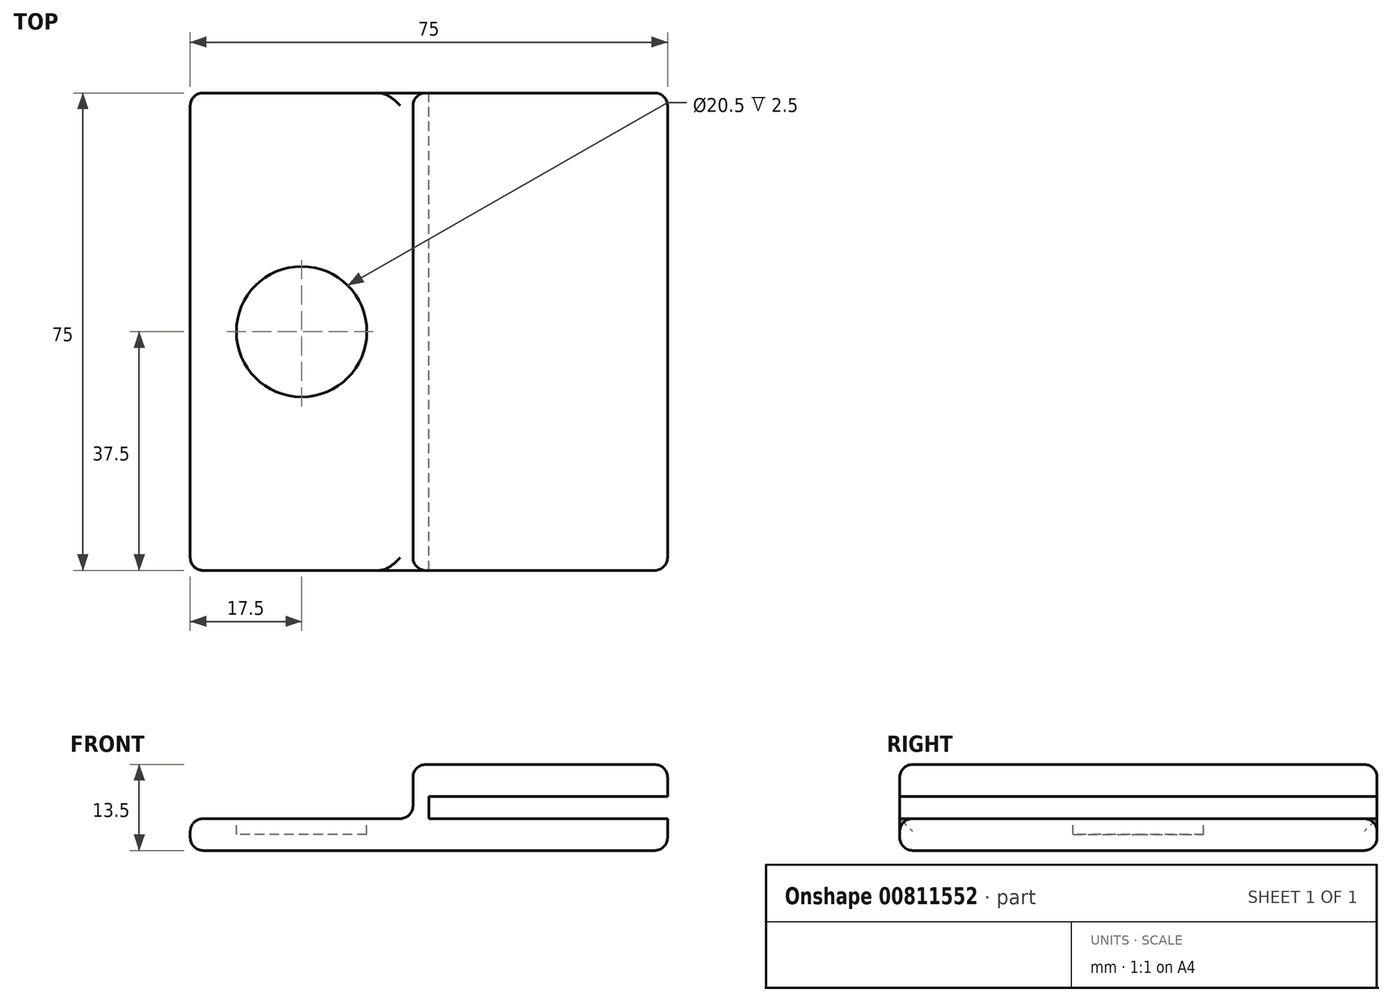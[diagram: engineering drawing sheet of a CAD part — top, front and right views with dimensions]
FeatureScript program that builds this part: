
annotation { "Feature Type Name" : "Feature", "Feature Type Description" : "" }
export const myFeature = defineFeature(function(context is Context, id is Id, definition is map)
    precondition{}
    {
        {
            var Q0;
            Q0=qCreatedBy(makeId("Top.planeOp"),FACE);
            var sketch = newSketch(context, id + "F0", { "sketchPlane" : qUnion([Q0])});
            skLineSegment(sketch, "E0.bottom", {"start": v(37.5, -37.5) * mm, "end": v(-37.5, -37.5) * mm});
            skLineSegment(sketch, "E0.top", {"start": v(37.5, 37.5) * mm, "end": v(-37.5, 37.5) * mm});
            skLineSegment(sketch, "E0.left", {"start": v(37.5, -37.5) * mm, "end": v(37.5, 37.5) * mm});
            skLineSegment(sketch, "E0.right", {"start": v(-37.5, -37.5) * mm, "end": v(-37.5, 37.5) * mm});
            skPoint(sketch, "E0.middle", {"position": v(0, 0) * mm});
            skSolve(sketch);
        }
        {
            var Q0;
            Q0 = qSketchRegion(id + "F0", true);
            extrude(context, id + "F1", {"entities" : qUnion([Q0]), "depth" : 5 * mm, "offsetDistance" : 25 * mm});
        }
        {
            var Q0;
            Q0=makeQuery(id+"F1.opExtrude","CAP_FACE",FACE,{"disambiguationData":[OSD([sQuery(id+"F0.wireOp",EDGE,"E0.bottom"),sQuery(id+"F0.wireOp",EDGE,"E0.top"),sQuery(id+"F0.wireOp",EDGE,"E0.left"),sQuery(id+"F0.wireOp",EDGE,"E0.right")])],"isStart":false});
            var sketch = newSketch(context, id + "F2", { "sketchPlane" : qUnion([Q0])});
            skLineSegment(sketch, "E1.bottom", {"start": v(-2.5, 37.5) * mm, "end": v(37.5, 37.5) * mm});
            skLineSegment(sketch, "E1.top", {"start": v(-2.5, -37.5) * mm, "end": v(37.5, -37.5) * mm});
            skLineSegment(sketch, "E1.left", {"start": v(-2.5, 37.5) * mm, "end": v(-2.5, -37.5) * mm});
            skLineSegment(sketch, "E1.right", {"start": v(37.5, 37.5) * mm, "end": v(37.5, -37.5) * mm});
            skSolve(sketch);
        }
        {
            var Q0;
            Q0 = qSketchRegion(id + "F2", true);
            extrude(context, id + "F3", {"entities" : qUnion([Q0]), "operationType" : NewBodyOperationType.ADD, "depth" : 8.5 * mm, "offsetDistance" : 25 * mm});
        }
        {
            var Q0;
            Q0=makeQuery(id+"F3.boolean.opBoolean","MERGE",FACE,{"derivedFrom":[makeQuery(id+"F1.opExtrude","SWEPT_FACE",FACE,{"disambiguationData":[OSD([sQuery(id+"F0.wireOp",EDGE,"E0.left")])]}),makeQuery(id+"F3.opExtrude","SWEPT_FACE",FACE,{"disambiguationData":[OSD([sQuery(id+"F2.wireOp",EDGE,"E1.right")])]})]});
            var sketch = newSketch(context, id + "F4", { "sketchPlane" : qUnion([Q0])});
            skLineSegment(sketch, "E2.bottom", {"start": v(37.5, 8.5) * mm, "end": v(-37.5, 8.5) * mm});
            skLineSegment(sketch, "E2.top", {"start": v(37.5, 5) * mm, "end": v(-37.5, 5) * mm});
            skLineSegment(sketch, "E2.left", {"start": v(37.5, 8.5) * mm, "end": v(37.5, 5) * mm});
            skLineSegment(sketch, "E2.right", {"start": v(-37.5, 8.5) * mm, "end": v(-37.5, 5) * mm});
            skSolve(sketch);
        }
        {
            var Q0;
            Q0 = qSketchRegion(id + "F4", true);
            var Q1;
            Q1=makeQuery(id+"F3.opExtrude","SWEPT_FACE",FACE,{"disambiguationData":[OSD([sQuery(id+"F2.wireOp",EDGE,"E1.left")])]});
            extrude(context, id + "F5", {"entities" : qUnion([Q0]), "operationType" : NewBodyOperationType.REMOVE, "endBound" : BoundingType.UP_TO_SURFACE, "oppositeDirection" : true, "depth" : 25 * mm, "endBoundEntityFace" : qUnion([Q1]), "hasOffset" : true, "offsetDistance" : 2.5 * mm});
        }
        {
            var Q0;
            Q0=makeQuery(id+"F1.opExtrude","CAP_FACE",FACE,{"disambiguationData":[OSD([sQuery(id+"F0.wireOp",EDGE,"E0.bottom"),sQuery(id+"F0.wireOp",EDGE,"E0.top"),sQuery(id+"F0.wireOp",EDGE,"E0.left"),sQuery(id+"F0.wireOp",EDGE,"E0.right")])],"isStart":false});
            var sketch = newSketch(context, id + "F6", { "sketchPlane" : qUnion([Q0])});
            skLineSegment(sketch, "E3", {"start": v(-20, 37.5) * mm, "end": v(-20, -37.5) * mm, "construction": true});
            skLineSegment(sketch, "E4", {"start": v(-37.5, 0) * mm, "end": v(-2.5, 0) * mm, "construction": true});
            skCircle(sketch, "E5", {"center": v(-20, 0) * mm, "radius": 10.25 * mm});
            skSolve(sketch);
        }
        {
            var Q0;
            Q0 = qSketchRegion(id + "F6", true);
            extrude(context, id + "F7", {"entities" : qUnion([Q0]), "operationType" : NewBodyOperationType.REMOVE, "oppositeDirection" : true, "depth" : 2.5 * mm, "offsetDistance" : 25 * mm});
        }
        {
            var Q0;
            Q0=makeQuery(id+"F3.opExtrude","CAP_FACE",FACE,{"disambiguationData":[OSD([sQuery(id+"F2.wireOp",EDGE,"E1.bottom"),sQuery(id+"F2.wireOp",EDGE,"E1.top"),sQuery(id+"F2.wireOp",EDGE,"E1.left"),sQuery(id+"F2.wireOp",EDGE,"E1.right")])],"isStart":false});
            var Q1;
            Q1=makeQuery(id+"F3.opExtrude","SWEPT_FACE",FACE,{"disambiguationData":[OSD([sQuery(id+"F2.wireOp",EDGE,"E1.left")])]});
            var Q2;
            Q2=makeQuery(id+"F1.opExtrude","SWEPT_FACE",FACE,{"disambiguationData":[OSD([sQuery(id+"F0.wireOp",EDGE,"E0.right")])]});
            var Q3;
            Q3=makeQuery(id+"F1.opExtrude","CAP_FACE",FACE,{"disambiguationData":[OSD([sQuery(id+"F0.wireOp",EDGE,"E0.bottom"),sQuery(id+"F0.wireOp",EDGE,"E0.top"),sQuery(id+"F0.wireOp",EDGE,"E0.left"),sQuery(id+"F0.wireOp",EDGE,"E0.right")])],"isStart":true});
            var Q4;
            {var subQ0=sQuery(id+"F2.wireOp",EDGE,"E1.top");var subQ1=sQuery(id+"F0.wireOp",EDGE,"E0.left");var subQ2=sQuery(id+"F2.wireOp",EDGE,"E1.right");var subQ3=sQuery(id+"F0.wireOp",EDGE,"E0.bottom");Q4=makeQuery(id+"F5.boolean.opBoolean","SPLIT",EDGE,{"disambiguationData":[TD([makeQuery(id+"F5.opExtrude","SWEPT_FACE",FACE,{"disambiguationData":[OSD([sQuery(id+"F4.wireOp",EDGE,"E2.bottom")])]})])],"derivedFrom":makeQuery(id+"F3.boolean.opBoolean","MERGE",EDGE,{"derivedFrom":[makeQuery(id+"F1.opExtrude","SWEPT_EDGE",EDGE,{"disambiguationData":[OSD([subQ3,subQ1])]}),makeQuery(id+"F3.opExtrude","SWEPT_EDGE",EDGE,{"disambiguationData":[OSD([subQ0,subQ2])]})]})});}
            var Q5;
            {var subQ0=sQuery(id+"F0.wireOp",EDGE,"E0.left");var subQ1=sQuery(id+"F2.wireOp",EDGE,"E1.top");var subQ2=sQuery(id+"F0.wireOp",EDGE,"E0.bottom");var subQ3=sQuery(id+"F2.wireOp",EDGE,"E1.right");Q5=makeQuery(id+"F5.boolean.opBoolean","SPLIT",EDGE,{"disambiguationData":[TD([makeQuery(id+"F5.opExtrude","SWEPT_FACE",FACE,{"disambiguationData":[OSD([sQuery(id+"F4.wireOp",EDGE,"E2.top")])]})])],"derivedFrom":makeQuery(id+"F3.boolean.opBoolean","MERGE",EDGE,{"derivedFrom":[makeQuery(id+"F1.opExtrude","SWEPT_EDGE",EDGE,{"disambiguationData":[OSD([subQ2,subQ0])]}),makeQuery(id+"F3.opExtrude","SWEPT_EDGE",EDGE,{"disambiguationData":[OSD([subQ1,subQ3])]})]})});}
            var Q6;
            {var subQ0=sQuery(id+"F2.wireOp",EDGE,"E1.right");var subQ1=sQuery(id+"F2.wireOp",EDGE,"E1.bottom");var subQ2=sQuery(id+"F0.wireOp",EDGE,"E0.top");var subQ3=sQuery(id+"F0.wireOp",EDGE,"E0.left");Q6=makeQuery(id+"F5.boolean.opBoolean","SPLIT",EDGE,{"disambiguationData":[TD([makeQuery(id+"F5.opExtrude","SWEPT_FACE",FACE,{"disambiguationData":[OSD([sQuery(id+"F4.wireOp",EDGE,"E2.bottom")])]})])],"derivedFrom":makeQuery(id+"F3.boolean.opBoolean","MERGE",EDGE,{"derivedFrom":[makeQuery(id+"F1.opExtrude","SWEPT_EDGE",EDGE,{"disambiguationData":[OSD([subQ2,subQ3])]}),makeQuery(id+"F3.opExtrude","SWEPT_EDGE",EDGE,{"disambiguationData":[OSD([subQ1,subQ0])]})]})});}
            var Q7;
            {var subQ0=sQuery(id+"F0.wireOp",EDGE,"E0.left");var subQ1=sQuery(id+"F2.wireOp",EDGE,"E1.bottom");var subQ2=sQuery(id+"F0.wireOp",EDGE,"E0.top");var subQ3=sQuery(id+"F2.wireOp",EDGE,"E1.right");Q7=makeQuery(id+"F5.boolean.opBoolean","SPLIT",EDGE,{"disambiguationData":[TD([makeQuery(id+"F5.opExtrude","SWEPT_FACE",FACE,{"disambiguationData":[OSD([sQuery(id+"F4.wireOp",EDGE,"E2.top")])]})])],"derivedFrom":makeQuery(id+"F3.boolean.opBoolean","MERGE",EDGE,{"derivedFrom":[makeQuery(id+"F1.opExtrude","SWEPT_EDGE",EDGE,{"disambiguationData":[OSD([subQ2,subQ0])]}),makeQuery(id+"F3.opExtrude","SWEPT_EDGE",EDGE,{"disambiguationData":[OSD([subQ1,subQ3])]})]})});}
            fillet(context, id + "F8", {"entities" : qUnion([Q0, Q1, Q2, Q3, Q4, Q5, Q6, Q7]), "radius" : 2 * mm, "tangentPropagation" : true, "allowEdgeOverflow" : false});
        }
    });
